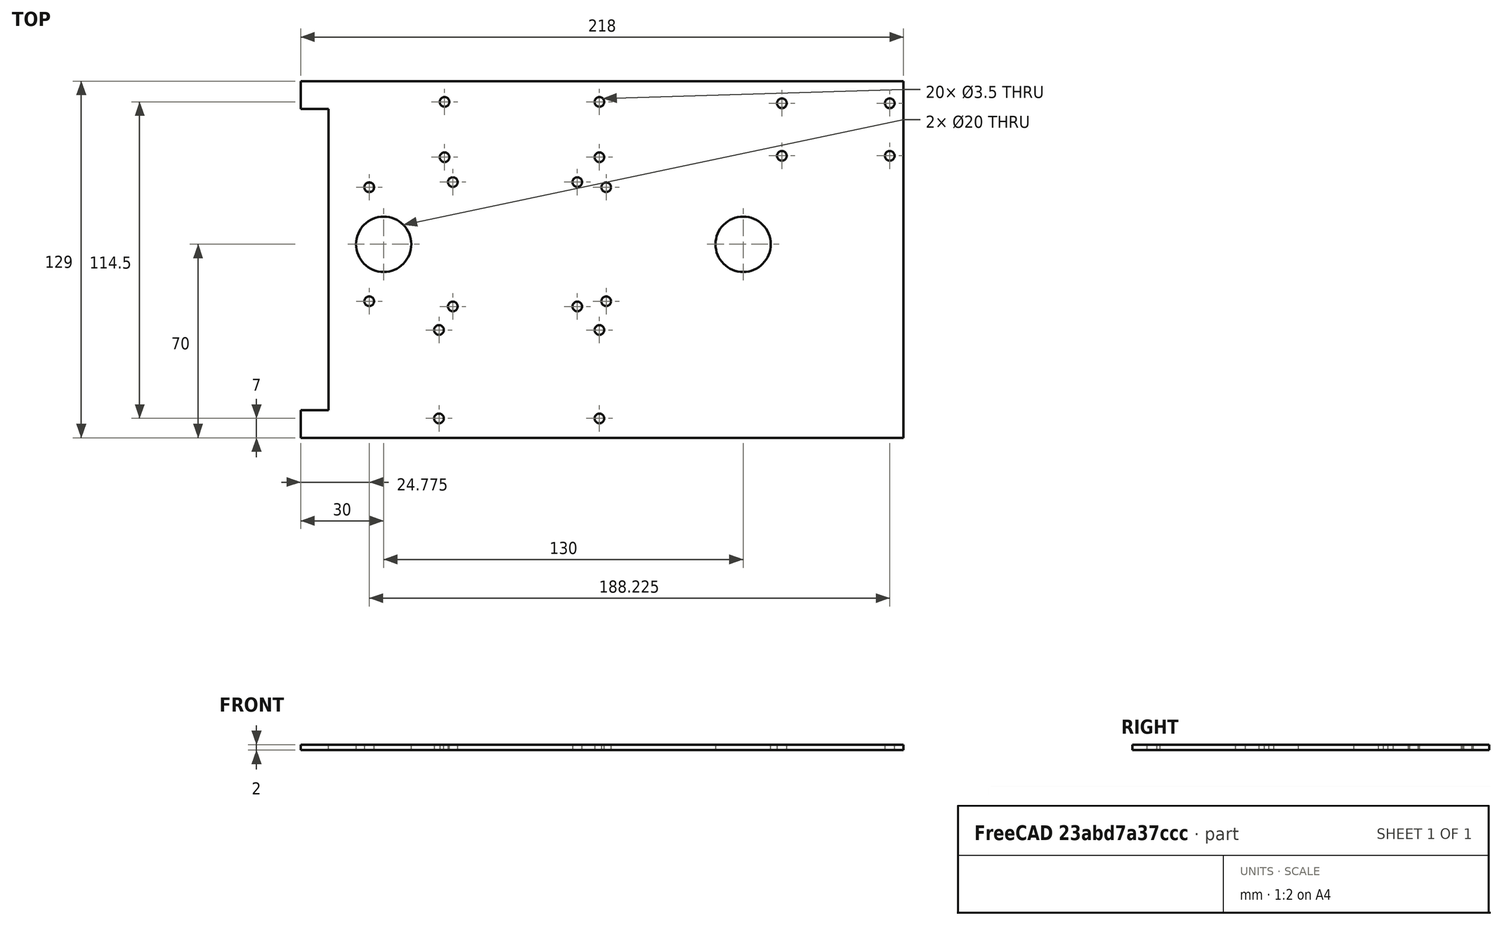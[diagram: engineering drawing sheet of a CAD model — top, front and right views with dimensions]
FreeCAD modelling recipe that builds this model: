
FCSTD DOCUMENT  (FreeCAD 0.20RUnknown)
Label: plate
License: All rights reserved
LicenseURL: http://en.wikipedia.org/wiki/All_rights_reserved
objects: Part::Cylinder×22, Part::Fuse×20, Part::Box×7, Part::MultiFuse×1, Part::Cut×1, TechDraw::DrawSVGTemplate×1, TechDraw::DrawViewPart×1, TechDraw::DrawPage×1
note: 51 computed .brp shape members not serialized (recipe doc carries the construction recipe); baked Part::Feature solids carry a one-line shape summary decoded from their .brp

FEATURE [Part::Box] cube
  AttacherType = Attacher::AttachEngine3D
  Height = 2
  Length = 218
  Placement = pos=(0,0,-2) rot=(0,0,1;0rad)
  Width = 129
FEATURE [Part::Box] cube001
  AttacherType = Attacher::AttachEngine3D
  Height = 12
  Length = 45
  Placement = pos=(-22.5,-12.5,0) rot=(0,0,1;0rad)
  Width = 25
FEATURE [Part::Cylinder] cylinder
  Angle = 360
  AttacherType = Attacher::AttachEngine3D
  FirstAngle = 0
  Height = 5
  Placement = pos=(-19.5,-9.5,-5) rot=(0,0,1;0rad)
  Radius = 1.75
  SecondAngle = 0
FEATURE [Part::Cylinder] cylinder001
  Angle = 360
  AttacherType = Attacher::AttachEngine3D
  FirstAngle = 0
  Height = 5
  Placement = pos=(-19.5,9.5,-5) rot=(0,0,1;0rad)
  Radius = 1.75
  SecondAngle = 0
FEATURE [Part::Fuse] Group
  Base = -> cylinder
  Tool = -> cylinder001
FEATURE [Part::Cylinder] cylinder002
  Angle = 360
  AttacherType = Attacher::AttachEngine3D
  FirstAngle = 0
  Height = 5
  Placement = pos=(19.5,-9.5,-5) rot=(0,0,1;0rad)
  Radius = 1.75
  SecondAngle = 0
FEATURE [Part::Cylinder] cylinder003
  Angle = 360
  AttacherType = Attacher::AttachEngine3D
  FirstAngle = 0
  Height = 5
  Placement = pos=(19.5,9.5,-5) rot=(0,0,1;0rad)
  Radius = 1.75
  SecondAngle = 0
FEATURE [Part::Fuse] Group001
  Base = -> cylinder002
  Tool = -> cylinder003
FEATURE [Part::Fuse] Group002
  Base = -> Group
  Tool = -> Group001
FEATURE [Part::Fuse] Group003
  Base = -> cube001
  Placement = pos=(193.5,111.5,0.1) rot=(0,0,1;0rad)
  Tool = -> Group002
FEATURE [Part::Box] cube002
  AttacherType = Attacher::AttachEngine3D
  Height = 17
  Length = 85
  Placement = pos=(-42.5,-13.5,0) rot=(0,0,1;0rad)
  Width = 27
FEATURE [Part::Cylinder] cylinder004
  Angle = 360
  AttacherType = Attacher::AttachEngine3D
  FirstAngle = 0
  Height = 5
  Placement = pos=(-28,-10,-5) rot=(0,0,1;0rad)
  Radius = 1.75
  SecondAngle = 0
FEATURE [Part::Cylinder] cylinder005
  Angle = 360
  AttacherType = Attacher::AttachEngine3D
  FirstAngle = 0
  Height = 5
  Placement = pos=(-28,10,-5) rot=(0,0,1;0rad)
  Radius = 1.75
  SecondAngle = 0
FEATURE [Part::Fuse] Group004
  Base = -> cylinder004
  Tool = -> cylinder005
FEATURE [Part::Cylinder] cylinder006
  Angle = 360
  AttacherType = Attacher::AttachEngine3D
  FirstAngle = 0
  Height = 5
  Placement = pos=(28,-10,-5) rot=(0,0,1;0rad)
  Radius = 1.75
  SecondAngle = 0
FEATURE [Part::Cylinder] cylinder007
  Angle = 360
  AttacherType = Attacher::AttachEngine3D
  FirstAngle = 0
  Height = 5
  Placement = pos=(28,10,-5) rot=(0,0,1;0rad)
  Radius = 1.75
  SecondAngle = 0
FEATURE [Part::Fuse] Group005
  Base = -> cylinder006
  Tool = -> cylinder007
FEATURE [Part::Fuse] Group006
  Base = -> Group004
  Tool = -> Group005
FEATURE [Part::Fuse] Group007
  Base = -> cube002
  Placement = pos=(80,111.5,0.1) rot=(0,0,1;0rad)
  Tool = -> Group006
FEATURE [Part::Box] cube003
  AttacherType = Attacher::AttachEngine3D
  Height = 20.32
  Length = 95.25
  Placement = pos=(-47.625,-25.4,0) rot=(0,0,1;0rad)
  Width = 50.8
FEATURE [Part::Cylinder] cylinder008
  Angle = 360
  AttacherType = Attacher::AttachEngine3D
  FirstAngle = 0
  Height = 5
  Placement = pos=(-42.85,-20.625,-5) rot=(0,0,1;0rad)
  Radius = 1.75
  SecondAngle = 0
FEATURE [Part::Cylinder] cylinder009
  Angle = 360
  AttacherType = Attacher::AttachEngine3D
  FirstAngle = 0
  Height = 5
  Placement = pos=(-42.85,20.625,-5) rot=(0,0,1;0rad)
  Radius = 1.75
  SecondAngle = 0
FEATURE [Part::Fuse] Group008
  Base = -> cylinder008
  Tool = -> cylinder009
FEATURE [Part::Cylinder] cylinder010
  Angle = 360
  AttacherType = Attacher::AttachEngine3D
  FirstAngle = 0
  Height = 5
  Placement = pos=(42.85,-20.625,-5) rot=(0,0,1;0rad)
  Radius = 1.75
  SecondAngle = 0
FEATURE [Part::Cylinder] cylinder011
  Angle = 360
  AttacherType = Attacher::AttachEngine3D
  FirstAngle = 0
  Height = 5
  Placement = pos=(42.85,20.625,-5) rot=(0,0,1;0rad)
  Radius = 1.75
  SecondAngle = 0
FEATURE [Part::Fuse] Group009
  Base = -> cylinder010
  Tool = -> cylinder011
FEATURE [Part::Fuse] Group010
  Base = -> Group008
  Tool = -> Group009
FEATURE [Part::Fuse] Group011
  Base = -> cube003
  Placement = pos=(67.625,70,0.1) rot=(0,0,1;0rad)
  Tool = -> Group010
FEATURE [Part::Box] cube004
  AttacherType = Attacher::AttachEngine3D
  Height = 10
  Length = 65
  Placement = pos=(-32.5,-19,0) rot=(0,0,1;0rad)
  Width = 38
FEATURE [Part::Cylinder] cylinder012
  Angle = 360
  AttacherType = Attacher::AttachEngine3D
  FirstAngle = 0
  Height = 5
  Placement = pos=(-29,-16,-5) rot=(0,0,1;0rad)
  Radius = 1.75
  SecondAngle = 0
FEATURE [Part::Cylinder] cylinder013
  Angle = 360
  AttacherType = Attacher::AttachEngine3D
  FirstAngle = 0
  Height = 5
  Placement = pos=(-29,16,-5) rot=(0,0,1;0rad)
  Radius = 1.75
  SecondAngle = 0
FEATURE [Part::Fuse] Group012
  Base = -> cylinder012
  Tool = -> cylinder013
FEATURE [Part::Cylinder] cylinder014
  Angle = 360
  AttacherType = Attacher::AttachEngine3D
  FirstAngle = 0
  Height = 5
  Placement = pos=(29,-16,-5) rot=(0,0,1;0rad)
  Radius = 1.75
  SecondAngle = 0
FEATURE [Part::Cylinder] cylinder015
  Angle = 360
  AttacherType = Attacher::AttachEngine3D
  FirstAngle = 0
  Height = 5
  Placement = pos=(29,16,-5) rot=(0,0,1;0rad)
  Radius = 1.75
  SecondAngle = 0
FEATURE [Part::Fuse] Group013
  Base = -> cylinder014
  Tool = -> cylinder015
FEATURE [Part::Fuse] Group014
  Base = -> Group012
  Tool = -> Group013
FEATURE [Part::Fuse] Group015
  Base = -> cube004
  Placement = pos=(79,23,0.1) rot=(0,0,1;0rad)
  Tool = -> Group014
FEATURE [Part::Box] cube005
  AttacherType = Attacher::AttachEngine3D
  Height = 10
  Length = 10
  Placement = pos=(0,10,-5) rot=(0,0,1;0rad)
  Width = 109
FEATURE [Part::Box] cube006
  AttacherType = Attacher::AttachEngine3D
  Height = 10
  Length = 55
  Placement = pos=(-27.5,-27.5,0) rot=(0,0,1;0rad)
  Width = 55
FEATURE [Part::Cylinder] cylinder016
  Angle = 360
  AttacherType = Attacher::AttachEngine3D
  FirstAngle = 0
  Height = 5
  Placement = pos=(-22.5,-22.5,-5) rot=(0,0,1;0rad)
  Radius = 1.75
  SecondAngle = 0
FEATURE [Part::Cylinder] cylinder017
  Angle = 360
  AttacherType = Attacher::AttachEngine3D
  FirstAngle = 0
  Height = 5
  Placement = pos=(-22.5,22.5,-5) rot=(0,0,1;0rad)
  Radius = 1.75
  SecondAngle = 0
FEATURE [Part::Fuse] Group016
  Base = -> cylinder016
  Tool = -> cylinder017
FEATURE [Part::Cylinder] cylinder018
  Angle = 360
  AttacherType = Attacher::AttachEngine3D
  FirstAngle = 0
  Height = 5
  Placement = pos=(22.5,-22.5,-5) rot=(0,0,1;0rad)
  Radius = 1.75
  SecondAngle = 0
FEATURE [Part::Cylinder] cylinder019
  Angle = 360
  AttacherType = Attacher::AttachEngine3D
  FirstAngle = 0
  Height = 5
  Placement = pos=(22.5,22.5,-5) rot=(0,0,1;0rad)
  Radius = 1.75
  SecondAngle = 0
FEATURE [Part::Fuse] Group017
  Base = -> cylinder018
  Tool = -> cylinder019
FEATURE [Part::Fuse] Group018
  Base = -> Group016
  Tool = -> Group017
FEATURE [Part::Fuse] Group019
  Base = -> cube006
  Placement = pos=(77.5,70,0.1) rot=(0,0,1;0rad)
  Tool = -> Group018
FEATURE [Part::Cylinder] cylinder020
  Angle = 360
  AttacherType = Attacher::AttachEngine3D
  FirstAngle = 0
  Height = 20
  Placement = pos=(160,70,-5) rot=(0,0,1;0rad)
  Radius = 10
  SecondAngle = 0
FEATURE [Part::Cylinder] cylinder021
  Angle = 360
  AttacherType = Attacher::AttachEngine3D
  FirstAngle = 0
  Height = 20
  Placement = pos=(30,70,-5) rot=(0,0,1;0rad)
  Radius = 10
  SecondAngle = 0
FEATURE [Part::MultiFuse] union
  Shapes = -> [Group003,Group007,Group011,Group015,cube005,Group019,cylinder020,cylinder021]
FEATURE [Part::Cut] difference
  Base = -> cube
  Tool = -> union
FEATURE [TechDraw::DrawSVGTemplate] Template
  Height = 210
  Orientation = 1
  Width = 297
FEATURE [TechDraw::DrawViewPart] View
  CoarseView = false
  Direction = (0,0,1)
  Focus = 100
  HardHidden = false
  IsoCount = 0
  IsoHidden = false
  IsoVisible = false
  LockPosition = false
  Perspective = false
  Rotation = 0
  ScaleType = 0
  SeamHidden = false
  SeamVisible = true
  SmoothHidden = false
  SmoothVisible = true
  Source = -> [difference]
  X = 148.5
  XDirection = (1,0,0)
  Y = 105
FEATURE [TechDraw::DrawPage] Page
  KeepUpdated = true
  NextBalloonIndex = 1
  ProjectionType = 0
  Template = -> Template
  Views = -> [View]
